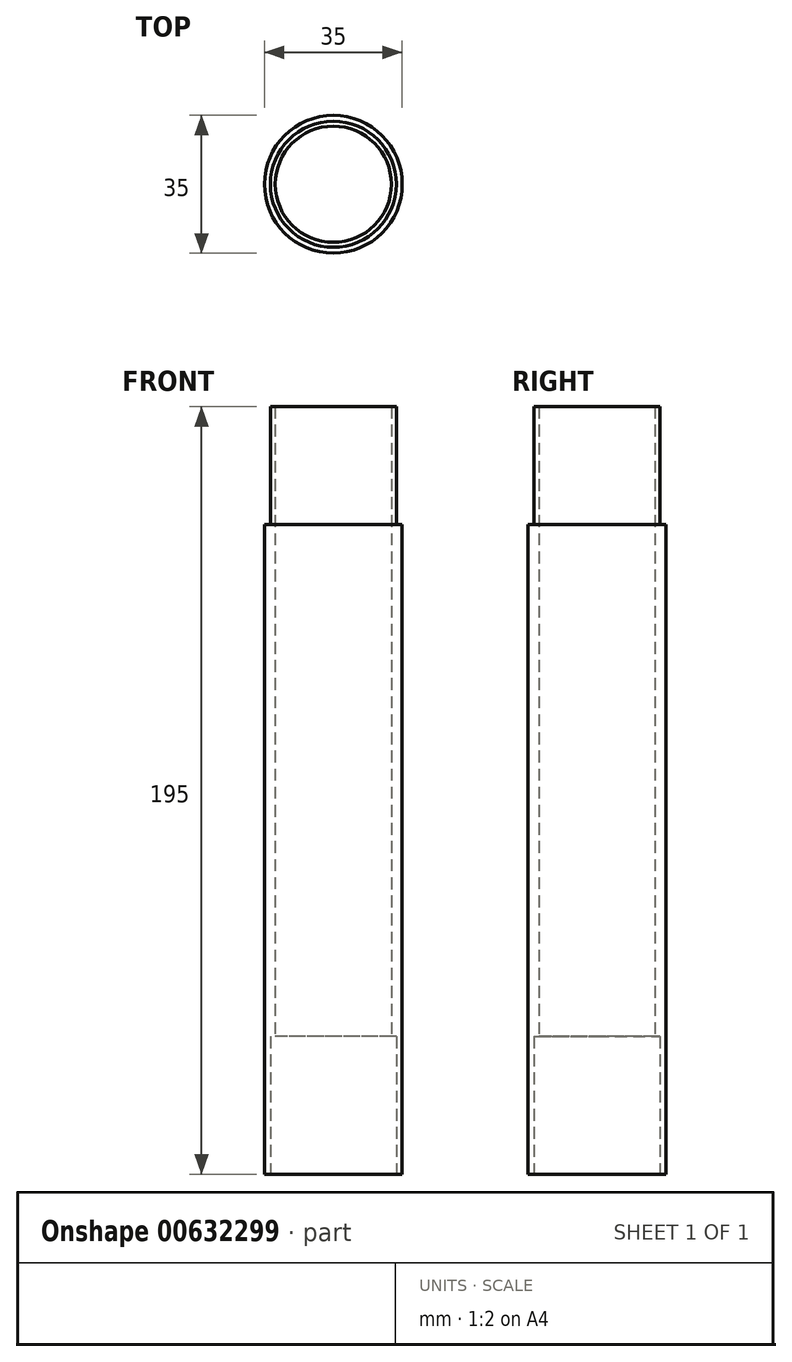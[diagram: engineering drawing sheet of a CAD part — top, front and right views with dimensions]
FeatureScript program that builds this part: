
annotation { "Feature Type Name" : "Feature", "Feature Type Description" : "" }
export const myFeature = defineFeature(function(context is Context, id is Id, definition is map)
    precondition{}
    {
        {
            var Q0;
            Q0=qCreatedBy(makeId("Top.planeOp"),FACE);
            var sketch = newSketch(context, id + "F0", { "sketchPlane" : qUnion([Q0])});
            skCircle(sketch, "E0", {"center": v(0, 0) * mm, "radius": 17.5 * mm});
            skCircle(sketch, "E1", {"center": v(0, 0) * mm, "radius": 14.75 * mm});
            skCircle(sketch, "E2", {"center": v(0, 0) * mm, "radius": 16 * mm});
            skSolve(sketch);
        }
        {
            var Q0;
            Q0=makeQuery(id+"F0.imprint","IMPRINT",FACE,{"disambiguationData":[TD([[makeQuery(id+"F0.imprint","IMPRINT",EDGE,{"derivedFrom":sQuery(id+"F0.wireOp",EDGE,"E1")}),-1.0]])]});
            extrude(context, id + "F1", {"entities" : qUnion([Q0]), "depth" : 195 * mm, "offsetDistance" : 25 * mm});
        }
        {
            var Q0;
            Q0=makeQuery(id+"F0.imprint","IMPRINT",FACE,{"disambiguationData":[TD([[makeQuery(id+"F0.imprint","IMPRINT",EDGE,{"derivedFrom":sQuery(id+"F0.wireOp",EDGE,"E0")}),1.0]])]});
            extrude(context, id + "F2", {"entities" : qUnion([Q0]), "operationType" : NewBodyOperationType.ADD, "depth" : 165 * mm, "offsetDistance" : 25 * mm});
        }
        {
            var Q0;
            Q0=makeQuery(id+"F0.imprint","IMPRINT",FACE,{"disambiguationData":[TD([[makeQuery(id+"F0.imprint","IMPRINT",EDGE,{"derivedFrom":sQuery(id+"F0.wireOp",EDGE,"E1")}),-1.0]])]});
            extrude(context, id + "F3", {"entities" : qUnion([Q0]), "operationType" : NewBodyOperationType.REMOVE, "depth" : 35 * mm, "offsetDistance" : 25 * mm});
        }
    });
